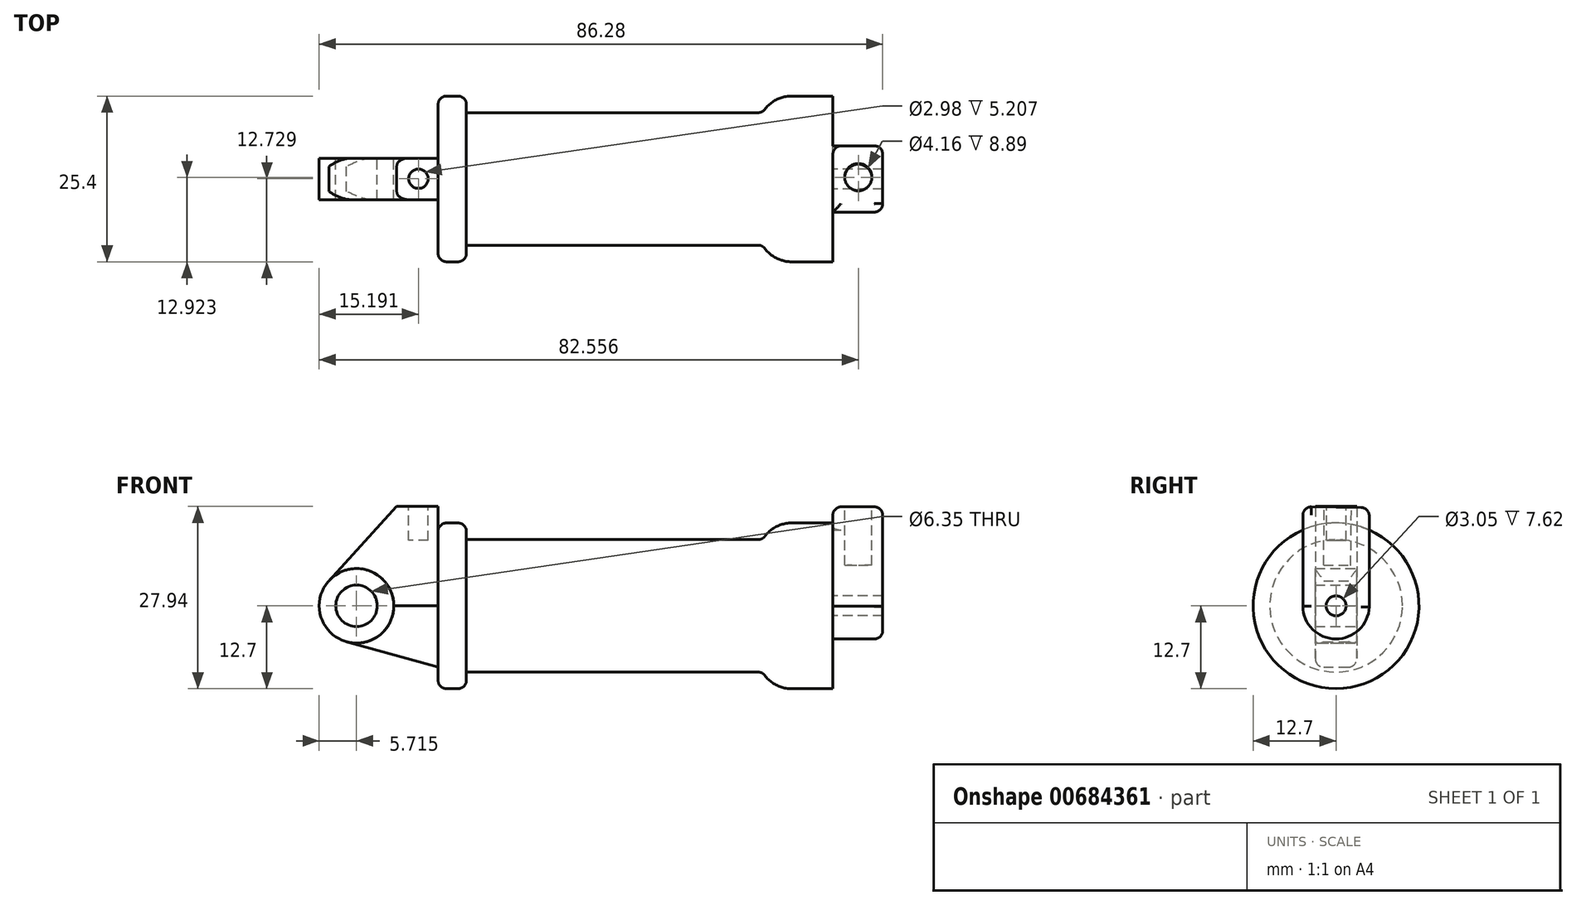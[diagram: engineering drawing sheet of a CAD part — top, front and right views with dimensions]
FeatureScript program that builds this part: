
annotation { "Feature Type Name" : "Feature", "Feature Type Description" : "" }
export const myFeature = defineFeature(function(context is Context, id is Id, definition is map)
    precondition{}
    {
        {
            var Q0;
            Q0=qCreatedBy(makeId("Front.planeOp"),FACE);
            var sketch = newSketch(context, id + "F0", { "sketchPlane" : qUnion([Q0])});
            skLineSegment(sketch, "E0", {"start": v(0, 0) * mm, "end": v(0, 12.7) * mm});
            skLineSegment(sketch, "E1", {"start": v(0, 12.7) * mm, "end": v(10.16, 12.7) * mm});
            skLineSegment(sketch, "E2", {"start": v(10.16, 12.7) * mm, "end": v(10.16, 10.16) * mm});
            skLineSegment(sketch, "E3", {"start": v(10.16, 10.16) * mm, "end": v(56.13, 10.16) * mm});
            skLineSegment(sketch, "E4", {"start": v(56.13, 10.16) * mm, "end": v(56.13, 12.7) * mm});
            skLineSegment(sketch, "E5", {"start": v(56.13, 12.7) * mm, "end": v(66.3, 12.7) * mm});
            skLineSegment(sketch, "E6", {"start": v(66.3, 12.7) * mm, "end": v(66.3, 0) * mm});
            skLineSegment(sketch, "E7", {"start": v(66.3, 0) * mm, "end": v(0, 0) * mm});
            skLineSegment(sketch, "E8", {"start": v(5.84, 15.24) * mm, "end": v(-0.5, 15.24) * mm});
            skLineSegment(sketch, "E9", {"start": v(-0.5, 15.24) * mm, "end": v(-10.88, 3.85) * mm});
            skLineSegment(sketch, "E10", {"start": v(0, 0) * mm, "end": v(-6.65, 0) * mm});
            skCircle(sketch, "E11", {"center": v(-6.65, 0) * mm, "radius": 5.72 * mm});
            skCircle(sketch, "E12", {"center": v(-6.65, 0) * mm, "radius": 3.18 * mm});
            skLineSegment(sketch, "E13", {"start": v(5.84, 15.24) * mm, "end": v(5.84, -9.4) * mm});
            skLineSegment(sketch, "E14", {"start": v(5.84, -9.4) * mm, "end": v(-8.18, -5.5) * mm});
            skSolve(sketch);
        }
        {
            var Q0;
            {var subQ0=sQuery(id+"F0.wireOp",EDGE,"E2");Q0=makeQuery(id+"F0.imprint","IMPRINT",FACE,{"disambiguationData":[TD([[makeQuery(id+"F0.imprint","IMPRINT",EDGE,{"derivedFrom":subQ0}),-1.0]])]});}
            var Q1;
            Q1=sQuery(id+"F0.wireOp",EDGE,"E7");
            revolve(context, id + "F1", {"entities" : qUnion([Q0]), "axis" : qUnion([Q1]), "revolveType" : RevolveType.FULL});
        }
        {
            var Q0;
            {var subQ0=sQuery(id+"F0.wireOp",EDGE,"E14");Q0=makeQuery(id+"F0.imprint","IMPRINT",FACE,{"disambiguationData":[TD([[makeQuery(id+"F0.imprint","IMPRINT",EDGE,{"derivedFrom":subQ0}),-1.0]])]});}
            extrude(context, id + "F2", {"entities" : qUnion([Q0]), "endBound" : BoundingType.SYMMETRIC, "depth" : 6.35 * mm, "offsetDistance" : 25.4 * mm});
        }
        {
            var Q0;
            {var subQ1=sQuery(id+"F0.wireOp",EDGE,"E0");Q0=makeQuery(id+"F0.imprint","IMPRINT",FACE,{"disambiguationData":[TD([[makeQuery(id+"F0.imprint","IMPRINT",EDGE,{"derivedFrom":subQ1}),1.0]])]});}
            var Q1;
            {var subQ0=sQuery(id+"F0.wireOp",EDGE,"E0");Q1=makeQuery(id+"F0.imprint","IMPRINT",FACE,{"disambiguationData":[TD([[makeQuery(id+"F0.imprint","IMPRINT",EDGE,{"derivedFrom":subQ0}),-1.0]])]});}
            extrude(context, id + "F3", {"entities" : qUnion([Q0, Q1]), "endBound" : BoundingType.SYMMETRIC, "depth" : 6.35 * mm, "offsetDistance" : 25.4 * mm});
        }
        {
            var Q0;
            {var subQ5=sQuery(id+"F0.wireOp",EDGE,"E12");Q0=makeQuery(id+"F0.imprint","IMPRINT",FACE,{"disambiguationData":[TD([[makeQuery(id+"F0.imprint","IMPRINT",EDGE,{"derivedFrom":subQ5}),-1.0]])]});}
            extrude(context, id + "F4", {"entities" : qUnion([Q0]), "endBound" : BoundingType.SYMMETRIC, "depth" : 6.35 * mm, "offsetDistance" : 25.4 * mm});
        }
        {
            var Q0;
            Q0=makeQuery(id+"F1.opRevolve","SWEPT_FACE",FACE,{"disambiguationData":[OSD([sQuery(id+"F0.wireOp",EDGE,"E6")])]});
            var sketch = newSketch(context, id + "F5", { "sketchPlane" : qUnion([Q0])});
            skCircle(sketch, "E15", {"center": v(0, 0) * mm, "radius": 1.52 * mm});
            skCircle(sketch, "E16", {"center": v(0, 0) * mm, "radius": 5.08 * mm});
            skLineSegment(sketch, "E17", {"start": v(5.08, -0.18) * mm, "end": v(5.08, 15.06) * mm});
            skLineSegment(sketch, "E18", {"start": v(-5.08, -0.05) * mm, "end": v(-5.08, 15.19) * mm});
            skLineSegment(sketch, "E19", {"start": v(-5.08, 15.19) * mm, "end": v(5.08, 15.06) * mm});
            skSolve(sketch);
        }
        {
            var Q0;
            {var subQ0=sQuery(id+"F5.wireOp",EDGE,"E18");var subQ1=sQuery(id+"F5.wireOp",EDGE,"E16");var subQ2=makeQuery(id+"F5.imprint","INTERSECT",VERTEX,{"derivedFrom":[subQ1,subQ0]});Q0=makeQuery(id+"F5.imprint","IMPRINT",FACE,{"disambiguationData":[TD([[makeQuery(id+"F5.imprint","IMPRINT",EDGE,{"disambiguationData":[TD([[subQ2,1.0]])],"derivedFrom":subQ1}),-1.0]])]});}
            var Q1;
            {var subQ0=sQuery(id+"F5.wireOp",EDGE,"E19");Q1=makeQuery(id+"F5.imprint","IMPRINT",FACE,{"disambiguationData":[TD([[makeQuery(id+"F5.imprint","IMPRINT",EDGE,{"derivedFrom":subQ0}),-1.0]])]});}
            var Q2;
            Q2=makeQuery(id+"F5.imprint","IMPRINT",FACE,{"disambiguationData":[TD([[makeQuery(id+"F5.imprint","IMPRINT",EDGE,{"derivedFrom":sQuery(id+"F5.wireOp",EDGE,"E15")}),-1.0]])]});
            extrude(context, id + "F6", {"entities" : qUnion([Q0, Q1, Q2]), "operationType" : NewBodyOperationType.ADD, "depth" : 7.62 * mm, "offsetDistance" : 25.4 * mm});
        }
        {
            var Q0;
            Q0=makeQuery(id+"F6.opExtrude","SWEPT_FACE",FACE,{"disambiguationData":[OSD([sQuery(id+"F5.wireOp",EDGE,"E19")])]});
            var sketch = newSketch(context, id + "F7", { "sketchPlane" : qUnion([Q0])});
            skCircle(sketch, "E20", {"center": v(70.19, 0.09) * mm, "radius": 2.08 * mm});
            skSolve(sketch);
        }
        {
            var Q0;
            Q0 = qSketchRegion(id + "F7", true);
            extrude(context, id + "F8", {"entities" : qUnion([Q0]), "operationType" : NewBodyOperationType.REMOVE, "endBound" : BoundingType.SYMMETRIC, "oppositeDirection" : true, "depth" : 17.78 * mm, "offsetDistance" : 25.4 * mm});
        }
        {
            var Q0;
            Q0=makeQuery(id+"F3.opExtrude","SWEPT_FACE",FACE,{"disambiguationData":[OSD([sQuery(id+"F0.wireOp",EDGE,"E8")])]});
            var sketch = newSketch(context, id + "F9", { "sketchPlane" : qUnion([Q0])});
            skCircle(sketch, "E21", {"center": v(2.82, 0.03) * mm, "radius": 1.49 * mm});
            skSolve(sketch);
        }
        {
            var Q0;
            Q0 = qSketchRegion(id + "F9", true);
            extrude(context, id + "F10", {"entities" : qUnion([Q0]), "operationType" : NewBodyOperationType.REMOVE, "endBound" : BoundingType.SYMMETRIC, "oppositeDirection" : true, "depth" : 10.4 * mm, "offsetDistance" : 25.4 * mm});
        }
        {
            var Q0;
            Q0=makeQuery(id+"F1.opRevolve","SWEPT_EDGE",EDGE,{"disambiguationData":[OSD([sQuery(id+"F0.wireOp",EDGE,"E1"),sQuery(id+"F0.wireOp",EDGE,"E2")])]});
            fillet(context, id + "F11", {"entities" : qUnion([Q0]), "radius" : 1.27 * mm, "tangentPropagation" : true, "allowEdgeOverflow" : false});
        }
        {
            var Q0;
            Q0=makeQuery(id+"F1.opRevolve","SWEPT_EDGE",EDGE,{"disambiguationData":[OSD([sQuery(id+"F0.wireOp",EDGE,"E3"),sQuery(id+"F0.wireOp",EDGE,"E4")])]});
            fillet(context, id + "F12", {"entities" : qUnion([Q0]), "radius" : 1.27 * mm, "tangentPropagation" : true, "allowEdgeOverflow" : false});
        }
        {
            var Q0;
            Q0=makeQuery(id+"F1.opRevolve","SWEPT_EDGE",EDGE,{"disambiguationData":[OSD([sQuery(id+"F0.wireOp",EDGE,"E4"),sQuery(id+"F0.wireOp",EDGE,"E5")])]});
            fillet(context, id + "F13", {"entities" : qUnion([Q0]), "radius" : 5.08 * mm, "tangentPropagation" : true, "allowEdgeOverflow" : false});
        }
        {
            var Q0;
            Q0=makeQuery(id+"F1.opRevolve","SWEPT_EDGE",EDGE,{"disambiguationData":[OSD([sQuery(id+"F0.wireOp",EDGE,"E1"),sQuery(id+"F0.wireOp",EDGE,"E13")])]});
            fillet(context, id + "F14", {"entities" : qUnion([Q0]), "radius" : 1.27 * mm, "tangentPropagation" : true, "allowEdgeOverflow" : false});
        }
        {
            var Q0;
            Q0=makeQuery(id+"F2.opExtrude","CAP_EDGE",EDGE,{"disambiguationData":[OSD([sQuery(id+"F0.wireOp",EDGE,"E14")])],"isStart":false});
            fillet(context, id + "F15", {"entities" : qUnion([Q0]), "radius" : 1.27 * mm, "tangentPropagation" : true, "allowEdgeOverflow" : false});
        }
        {
            var Q0;
            Q0=makeQuery(id+"F2.opExtrude","CAP_EDGE",EDGE,{"disambiguationData":[OSD([sQuery(id+"F0.wireOp",EDGE,"E14")])],"isStart":true});
            fillet(context, id + "F16", {"entities" : qUnion([Q0]), "radius" : 1.27 * mm, "tangentPropagation" : true, "allowEdgeOverflow" : false});
        }
        {
            var Q0;
            Q0=makeQuery(id+"F3.opExtrude","CAP_EDGE",EDGE,{"disambiguationData":[OSD([sQuery(id+"F0.wireOp",EDGE,"E9")])],"isStart":false});
            var Q1;
            Q1=makeQuery(id+"F3.opExtrude","CAP_EDGE",EDGE,{"disambiguationData":[OSD([sQuery(id+"F0.wireOp",EDGE,"E9")])],"isStart":true});
            fillet(context, id + "F17", {"entities" : qUnion([Q0, Q1]), "radius" : 1.27 * mm, "tangentPropagation" : true, "allowEdgeOverflow" : false});
        }
        {
            var Q0;
            Q0=makeQuery(id+"F6.opExtrude","CAP_EDGE",EDGE,{"disambiguationData":[OSD([sQuery(id+"F5.wireOp",EDGE,"E18")])],"isStart":false});
            var Q1;
            Q1=makeQuery(id+"F6.opExtrude","CAP_EDGE",EDGE,{"disambiguationData":[OSD([sQuery(id+"F5.wireOp",EDGE,"E17")])],"isStart":false});
            var Q2;
            Q2=makeQuery(id+"F6.opExtrude","CAP_EDGE",EDGE,{"disambiguationData":[OSD([sQuery(id+"F5.wireOp",EDGE,"E19")])],"isStart":false});
            var Q3;
            Q3=makeQuery(id+"F6.opExtrude","SWEPT_EDGE",EDGE,{"disambiguationData":[OSD([sQuery(id+"F5.wireOp",EDGE,"E17"),sQuery(id+"F5.wireOp",EDGE,"E19")])]});
            var Q4;
            Q4=makeQuery(id+"F6.opExtrude","CAP_EDGE",EDGE,{"disambiguationData":[OSD([sQuery(id+"F5.wireOp",EDGE,"E16")])],"isStart":false});
            fillet(context, id + "F18", {"entities" : qUnion([Q0, Q1, Q2, Q3, Q4]), "radius" : 1.27 * mm, "tangentPropagation" : true, "allowEdgeOverflow" : false});
        }
        {
            var Q0;
            Q0=makeQuery(id+"F6.opExtrude","SWEPT_EDGE",EDGE,{"disambiguationData":[OSD([sQuery(id+"F5.wireOp",EDGE,"E18"),sQuery(id+"F5.wireOp",EDGE,"E19")])]});
            var Q1;
            Q1=makeQuery(id+"F6.opExtrude","CAP_EDGE",EDGE,{"disambiguationData":[OSD([sQuery(id+"F5.wireOp",EDGE,"E19")])],"isStart":true});
            fillet(context, id + "F19", {"entities" : qUnion([Q0, Q1]), "radius" : 1.27 * mm, "tangentPropagation" : true, "allowEdgeOverflow" : false});
        }
    });
